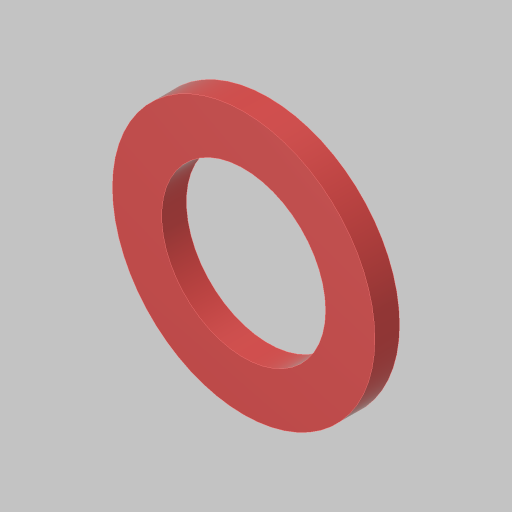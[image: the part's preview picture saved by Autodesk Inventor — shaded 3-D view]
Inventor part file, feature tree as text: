
AUTODESK INVENTOR PART (.ipt)
format: ipt  version: 2023.5 (Build 275446000, 446)  size: 101,376 bytes
history: native  units: in
note: dims shown in document units (in); Inventor stores cm internally (conversion verified against a paired STEP export)
features: extrude x1, sketch x1
ambient origin geometry x8: Origin, YZ Plane, XZ Plane, XY Plane, X Axis, Y Axis, Z Axis, Center Point
bodies: Solid1 (feature_tree)
feature tree (2):
  extrude  "Extrusion1"  Depth=0.0625in
  sketch  "Sketch1"  dims[d0=0.125in d1=0.415in d2=0.0625in d3=0.0in]
